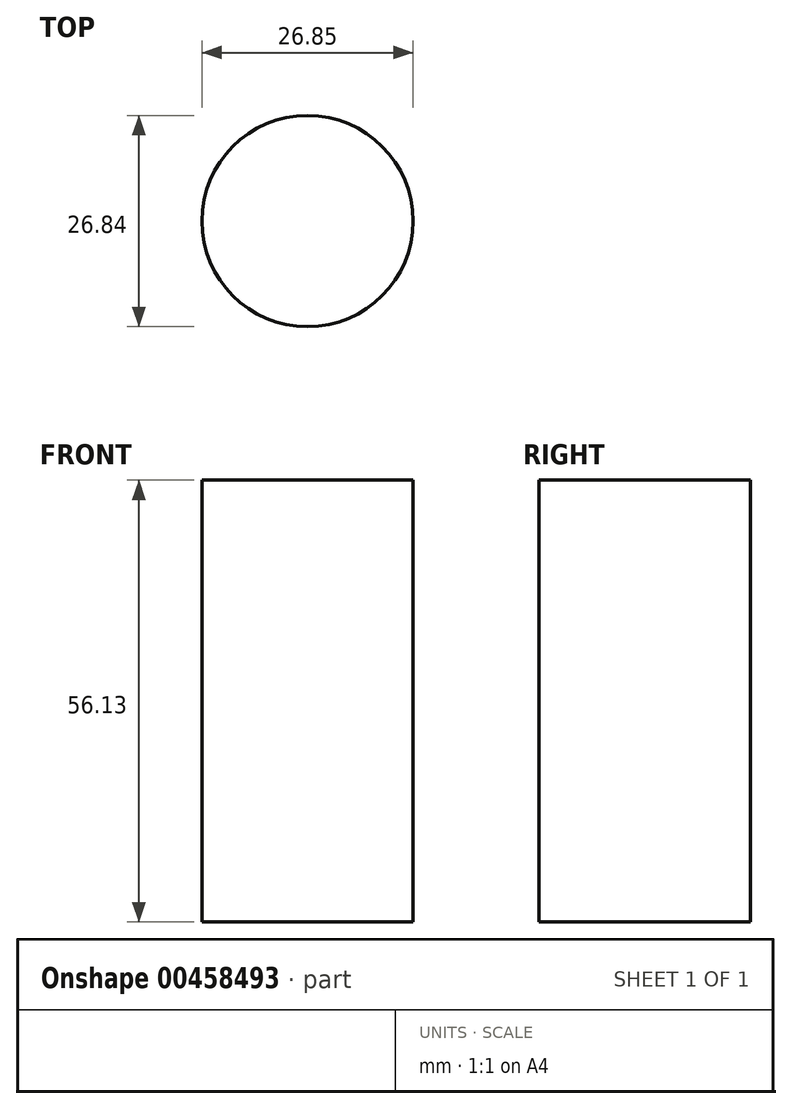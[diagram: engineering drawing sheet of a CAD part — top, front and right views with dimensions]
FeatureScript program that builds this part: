
annotation { "Feature Type Name" : "Feature", "Feature Type Description" : "" }
export const myFeature = defineFeature(function(context is Context, id is Id, definition is map)
    precondition{}
    {
        {
            var Q0;
            Q0=qCreatedBy(makeId("Top.planeOp"),FACE);
            var sketch = newSketch(context, id + "F0", { "sketchPlane" : qUnion([Q0])});
            skCircle(sketch, "E0", {"center": v(-50, -9.58) * mm, "radius": 13.42 * mm});
            skSolve(sketch);
        }
        {
            var Q0;
            Q0=makeQuery(id+"F0.imprint","IMPRINT",FACE,{"disambiguationData":[TD([[makeQuery(id+"F0.imprint","IMPRINT",EDGE,{"derivedFrom":sQuery(id+"F0.wireOp",EDGE,"E0")}),1.0]])]});
            extrude(context, id + "F1", {"entities" : qUnion([Q0]), "depth" : 56.13 * mm});
        }
    });
